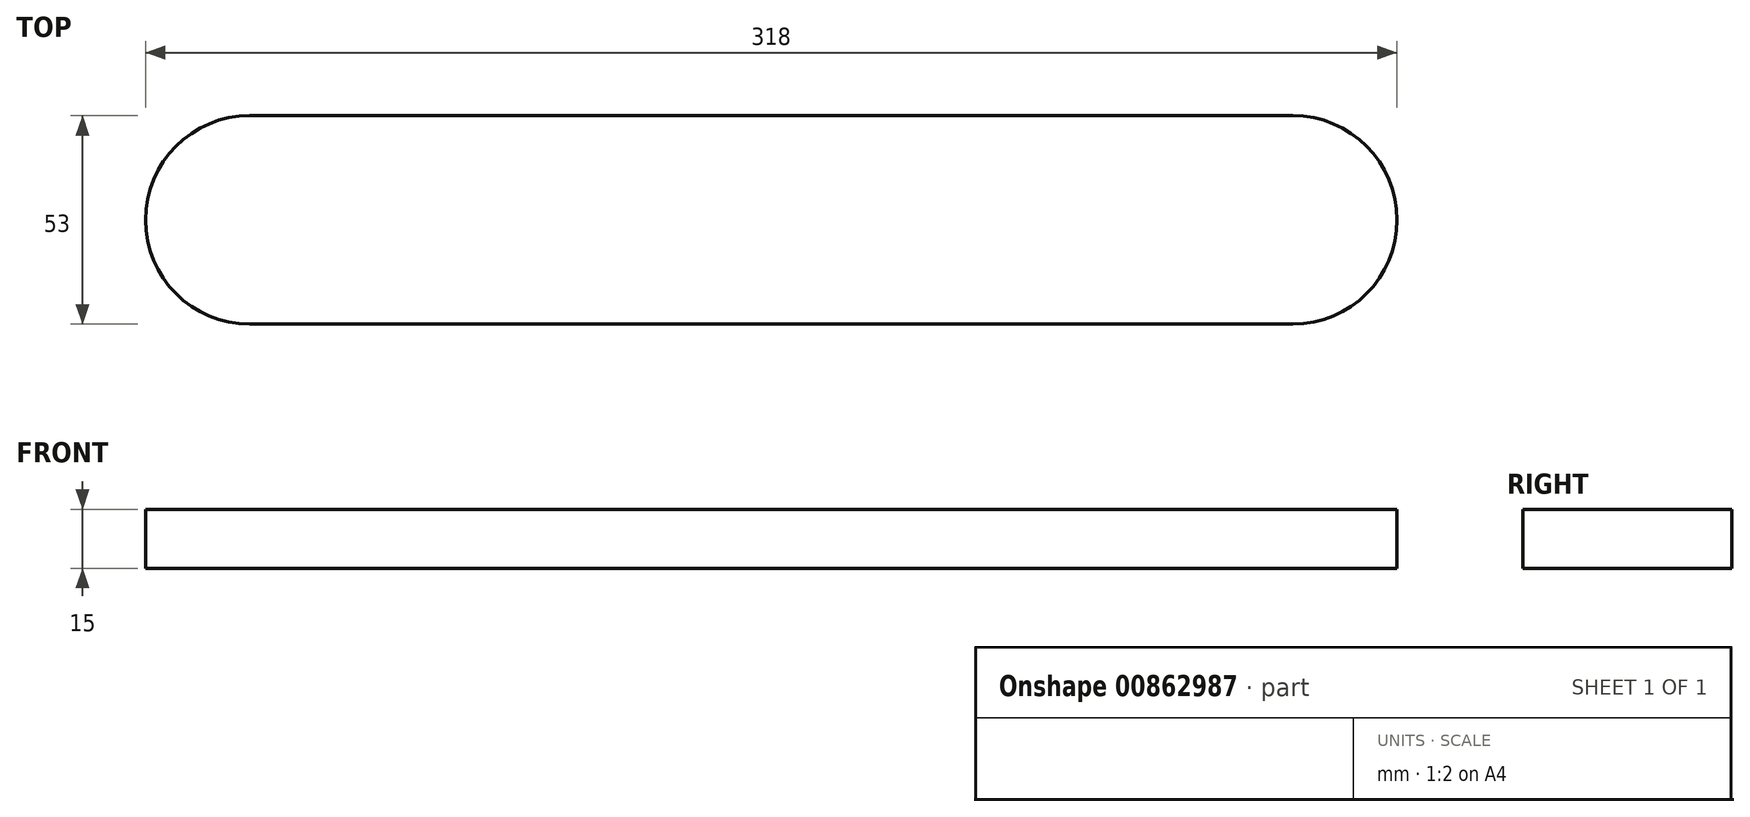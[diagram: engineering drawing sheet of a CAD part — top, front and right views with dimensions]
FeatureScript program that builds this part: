
annotation { "Feature Type Name" : "Feature", "Feature Type Description" : "" }
export const myFeature = defineFeature(function(context is Context, id is Id, definition is map)
    precondition{}
    {
        {
            var Q0;
            Q0=qCreatedBy(makeId("Top.planeOp"),FACE);
            var sketch = newSketch(context, id + "F0", { "sketchPlane" : qUnion([Q0])});
            skLineSegment(sketch, "E0.bottom", {"start": v(132.5, 26.5) * mm, "end": v(-132.5, 26.5) * mm});
            skLineSegment(sketch, "E0.top", {"start": v(132.5, -26.5) * mm, "end": v(-132.5, -26.5) * mm});
            skPoint(sketch, "E0.middle", {"position": v(0, 0) * mm});
            skArc(sketch, "E1", {"start": v(-132.5, 26.5) * mm, "mid": v(-159, 0) * mm, "end": v(-132.5, -26.5) * mm});
            skArc(sketch, "E2", {"start": v(132.5, 26.5) * mm, "mid": v(159, 0) * mm, "end": v(132.5, -26.5) * mm});
            skSolve(sketch);
        }
        {
            var Q0;
            Q0 = qSketchRegion(id + "F0", true);
            extrude(context, id + "F1", {"entities" : qUnion([Q0]), "flatOperationType" : FlatOperationType.REMOVE, "depth" : 15 * mm, "offsetDistance" : 25 * mm, "domain" : OperationDomain.MODEL});
        }
    });
